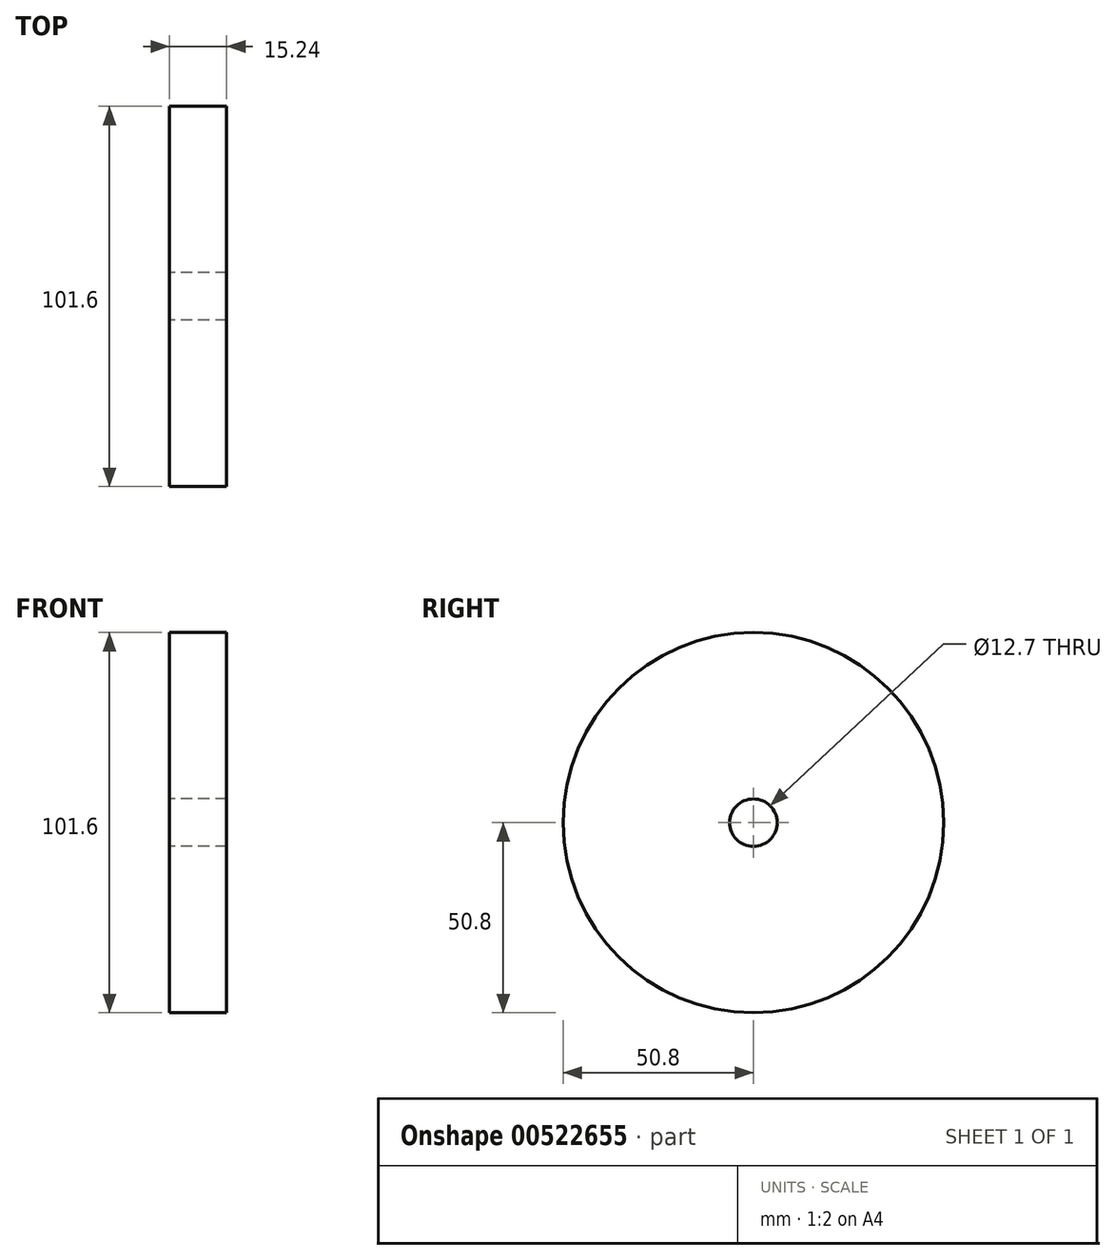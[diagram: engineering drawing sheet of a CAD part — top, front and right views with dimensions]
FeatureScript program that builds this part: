
annotation { "Feature Type Name" : "Feature", "Feature Type Description" : "" }
export const myFeature = defineFeature(function(context is Context, id is Id, definition is map)
    precondition{}
    {
        {
            var Q0;
            Q0=qCreatedBy(makeId("Top.planeOp"),FACE);
            var sketch = newSketch(context, id + "F0", { "sketchPlane" : qUnion([Q0])});
            skLineSegment(sketch, "E0.bottom", {"start": v(-15.77, 50.8) * mm, "end": v(-0.53, 50.8) * mm});
            skLineSegment(sketch, "E0.top", {"start": v(-15.77, 6.35) * mm, "end": v(-0.53, 6.35) * mm});
            skLineSegment(sketch, "E0.left", {"start": v(-15.77, 50.8) * mm, "end": v(-15.77, 6.35) * mm});
            skLineSegment(sketch, "E0.right", {"start": v(-0.53, 50.8) * mm, "end": v(-0.53, 6.35) * mm});
            skLineSegment(sketch, "E1.bottom", {"start": v(-0.53, 6.35) * mm, "end": v(-15.77, 6.35) * mm});
            skLineSegment(sketch, "E1.top", {"start": v(-0.53, 0) * mm, "end": v(-15.77, 0) * mm});
            skLineSegment(sketch, "E1.left", {"start": v(-0.53, 6.35) * mm, "end": v(-0.53, 0) * mm});
            skLineSegment(sketch, "E1.right", {"start": v(-15.77, 6.35) * mm, "end": v(-15.77, 0) * mm});
            skLineSegment(sketch, "E2.bottom", {"start": v(-0.53, 6.35) * mm, "end": v(14.7, 6.35) * mm});
            skLineSegment(sketch, "E2.top", {"start": v(-0.53, 0) * mm, "end": v(14.7, 0) * mm});
            skLineSegment(sketch, "E2.right", {"start": v(14.7, 6.35) * mm, "end": v(14.7, 0) * mm});
            skLineSegment(sketch, "E3.bottom", {"start": v(14.7, 6.35) * mm, "end": v(-0.53, 6.35) * mm});
            skLineSegment(sketch, "E3.top", {"start": v(14.7, 15.16) * mm, "end": v(-0.53, 15.16) * mm});
            skLineSegment(sketch, "E3.left", {"start": v(14.7, 6.35) * mm, "end": v(14.7, 15.16) * mm});
            skLineSegment(sketch, "E3.right", {"start": v(-0.53, 6.35) * mm, "end": v(-0.53, 15.16) * mm});
            skSolve(sketch);
        }
        {
            var Q0;
            Q0=makeQuery(id+"F0.imprint","IMPRINT",FACE,{"disambiguationData":[TD([[makeQuery(id+"F0.imprint","IMPRINT",EDGE,{"derivedFrom":sQuery(id+"F0.wireOp",EDGE,"E0.bottom")}),-1.0]])]});
            var Q1;
            Q1=makeQuery(id+"F0.imprint","IMPRINT",FACE,{"disambiguationData":[TD([[makeQuery(id+"F0.imprint","IMPRINT",EDGE,{"derivedFrom":sQuery(id+"F0.wireOp",EDGE,"E3.bottom")}),-1.0]])]});
            var Q2;
            Q2=sQuery(id+"F0.wireOp",EDGE,"E2.top");
            revolve(context, id + "F1", {"entities" : qUnion([Q0, Q1]), "axis" : qUnion([Q2]), "revolveType" : RevolveType.FULL});
        }
    });
